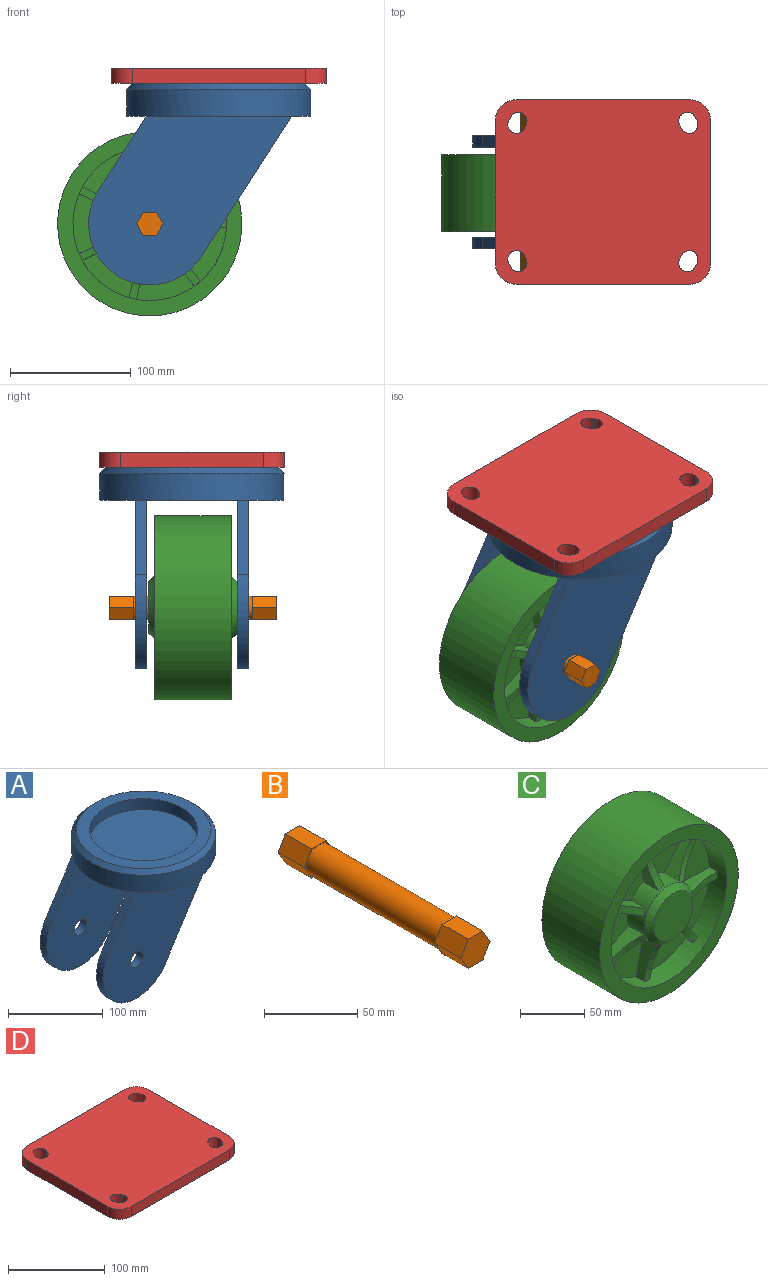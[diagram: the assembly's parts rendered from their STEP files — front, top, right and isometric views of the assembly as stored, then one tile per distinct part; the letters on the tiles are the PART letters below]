
ASSEMBLY  parts=4 mates=3
PART A: 20 faces, bbox 183.9x152.4x166.5 mm
  f0: plane 61.55x39.57mm, normal (-0.84,0,0.54), area 696.9mm2, adj f1,f3,f4,f5
  f1: cylinder r=50.58mm len=93.14mm, axis (0,1,0), area 1513.7mm2, adj f0,f2,f3,f4
  f2: plane 116.25x74.73mm, normal (0.84,0,-0.54), area 1316.4mm2, adj f1,f3,f4,f5
  f3: plane 167.87x139.48mm, normal (0,-1,0), area 14426.4mm2, adj f0,f1,f2,f8,f12
  f4: plane 167.87x139.48mm, normal (0,1,0), area 14426.4mm2, adj f0,f1,f2,f5,f12
  f5: plane 152.4x93.6mm, normal (0,0,-1), area 11017.4mm2, adj f0,f2,f4,f6,f13,f15,f17
  f6: cylinder r=76.2mm len=152.4mm, axis (0,0,-1), area 10519.2mm2, adj f5,f8,f11,f18
  f7: plane 114.3x114.3mm, normal (0,0,1), area 10260.8mm2, adj f9
  f8: plane 120.27x29.4mm, normal (0,0,-1), area 2466.5mm2, adj f3,f6
  f9: cylinder r=57.15mm len=114.3mm, axis (0,0,-1), area 5153.2mm2, adj f7,f10
  f10: plane 142.24x142.24mm, normal (0,0,1), area 5629.5mm2, adj f9,f11
  f11: cone r=76.2mm half-angle=45deg, axis (0,0,-1), area 3325mm2, adj f6,f10
  f12: cylinder r=9.53mm len=19.05mm, axis (0,1,0), area 570mm2, adj f3,f4
  f13: plane 61.55x39.57mm, normal (-0.84,0,0.54), area 696.9mm2, adj f5,f14,f16,f17
  f14: cylinder r=50.58mm len=93.14mm, axis (0,-1,0), area 1513.7mm2, adj f13,f15,f16,f17
  f15: plane 116.25x74.73mm, normal (0.84,0,-0.54), area 1316.4mm2, adj f5,f14,f16,f17
  f16: plane 167.87x139.48mm, normal (0,1,0), area 14426.4mm2, adj f13,f14,f15,f18,f19
  f17: plane 167.87x139.48mm, normal (0,-1,0), area 14426.4mm2, adj f5,f13,f14,f15,f19
  f18: plane 120.27x29.4mm, normal (0,0,-1), area 2466.5mm2, adj f6,f16
  f19: cylinder r=9.53mm len=19.05mm, axis (0,-1,0), area 570mm2, adj f16,f17
PART B: 17 faces, bbox 22x138.4x19.1 mm
  f0: cylinder r=9.5mm len=98.68mm, axis (0,1,0), area 5889.9mm2, adj f8,f16
  f1: plane 19.84x9.53mm, normal (0.87,0,0.5), area 218.3mm2, adj f2,f6,f7,f8
  f2: plane 19.84x11mm, normal (0,0,1), area 218.3mm2, adj f1,f3,f7,f8
  f3: plane 19.84x9.53mm, normal (-0.87,0,0.5), area 218.3mm2, adj f2,f4,f7,f8
  f4: plane 19.84x9.53mm, normal (-0.87,0,-0.5), area 218.3mm2, adj f3,f5,f7,f8
  f5: plane 19.84x11mm, normal (0,0,-1), area 218.3mm2, adj f4,f6,f7,f8
  f6: plane 19.84x9.53mm, normal (0.87,0,-0.5), area 218.3mm2, adj f1,f5,f7,f8
  f7: plane 22x19.05mm, normal (0,-1,0), area 314.3mm2, adj f1,f2,f3,f4,f5,f6
  f8: plane 22x19.05mm, normal (0,1,0), area 30.8mm2, adj f0,f1,f2,f3,f4,f5,f6
  f9: plane 19.84x9.53mm, normal (0.87,0,0.5), area 218.3mm2, adj f10,f14,f15,f16
  f10: plane 19.84x11mm, normal (0,0,1), area 218.3mm2, adj f9,f11,f15,f16
  f11: plane 19.84x9.53mm, normal (-0.87,0,0.5), area 218.3mm2, adj f10,f12,f15,f16
  f12: plane 19.84x9.53mm, normal (-0.87,0,-0.5), area 218.3mm2, adj f11,f13,f15,f16
  f13: plane 19.84x11mm, normal (0,0,-1), area 218.3mm2, adj f12,f14,f15,f16
  f14: plane 19.84x9.53mm, normal (0.87,0,-0.5), area 218.3mm2, adj f9,f13,f15,f16
  f15: plane 22x19.05mm, normal (0,1,0), area 314.3mm2, adj f9,f10,f11,f12,f13,f14
  f16: plane 22x19.05mm, normal (0,-1,0), area 30.8mm2, adj f0,f9,f10,f11,f12,f13,f14
PART C: 67 faces, bbox 152.4x73x152.4 mm
  f0: plane 48.08x40.82mm, normal (0,-1,0), area 1256.3mm2, adj f7,f9,f27,f32
  f1: plane 46.77x46.77mm, normal (0,-1,0), area 1256.3mm2, adj f7,f9,f24,f29
  f2: plane 49.31x38.26mm, normal (0,-1,0), area 1256.3mm2, adj f7,f9,f21,f26
  f3: plane 46.77x46.77mm, normal (0,-1,0), area 1256.3mm2, adj f7,f9,f18,f23
  f4: plane 48.08x40.82mm, normal (0,-1,0), area 1256.3mm2, adj f7,f9,f15,f20
  f5: plane 44.43x44.43mm, normal (0,-1,0), area 1256.3mm2, adj f7,f9,f13,f17
  f6: plane 43.18x43.18mm, normal (0,-1,0), area 1464.4mm2, adj f33
  f7: cylinder r=26.67mm len=53.34mm, axis (0,1,0), area 2416.2mm2, adj f0,f1,f2,f3,f4,f5,f8,f12
  f8: plane 44.43x44.43mm, normal (0,-1,0), area 1256.3mm2, adj f7,f9,f14,f30
  f9: cylinder r=63.5mm len=127mm, axis (0,1,0), area 7205.5mm2, adj f0,f1,f2,f3,f4,f5,f8,f10
  f10: plane 152.4x152.4mm, normal (0,-1,0), area 5573.8mm2, adj f9,f11
  f11: cylinder r=76.2mm len=152.4mm, axis (0,1,0), area 30402.4mm2, adj f10,f44
  f12: cylinder r=76.2mm len=37.02mm, axis (0,0,-1), area 241.2mm2, adj f7,f9,f13,f14
  f13: plane 36.94x16.28mm, normal (0,0,1), area 405.3mm2, adj f5,f7,f9,f12
  f14: plane 36.94x16.28mm, normal (0,0,-1), area 405.3mm2, adj f7,f8,f9,f12
  f15: plane 28.88x23.03mm, normal (-0.78,0,0.62), area 405.3mm2, adj f4,f7,f9,f16
  f16: cylinder r=76.2mm len=32.9mm, axis (0.78,0,-0.62), area 241.2mm2, adj f7,f9,f15,f17
  f17: plane 28.88x23.03mm, normal (0.78,0,-0.62), area 405.3mm2, adj f5,f7,f9,f16
  f18: plane 36.01x16.28mm, normal (-0.97,0,-0.22), area 405.3mm2, adj f3,f7,f9,f19
  f19: cylinder r=76.2mm len=37.5mm, axis (0.97,0,0.22), area 241.2mm2, adj f7,f9,f18,f20
  f20: plane 36.01x16.28mm, normal (0.97,0,0.22), area 405.3mm2, adj f4,f7,f9,f19
  f21: plane 33.28x16.28mm, normal (-0.43,0,-0.9), area 405.3mm2, adj f2,f7,f9,f22
  f22: cylinder r=76.2mm len=36.11mm, axis (0.43,0,0.9), area 241.2mm2, adj f7,f9,f21,f23
  f23: plane 33.28x16.28mm, normal (0.43,0,0.9), area 405.3mm2, adj f3,f7,f9,f22
  f24: plane 33.28x16.28mm, normal (0.43,0,-0.9), area 405.3mm2, adj f1,f7,f9,f25
  f25: cylinder r=76.2mm len=36.11mm, axis (-0.43,0,0.9), area 241.2mm2, adj f7,f9,f24,f26
  f26: plane 33.28x16.28mm, normal (-0.43,0,0.9), area 405.3mm2, adj f2,f7,f9,f25
  f27: plane 36.01x16.28mm, normal (0.97,0,-0.22), area 405.3mm2, adj f0,f7,f9,f28
  f28: cylinder r=76.2mm len=37.5mm, axis (-0.97,0,0.22), area 241.2mm2, adj f7,f9,f27,f29
  f29: plane 36.01x16.28mm, normal (-0.97,0,0.22), area 405.3mm2, adj f1,f7,f9,f28
  f30: plane 28.88x23.03mm, normal (0.78,0,0.62), area 405.3mm2, adj f7,f8,f9,f31
  f31: cylinder r=76.2mm len=32.9mm, axis (-0.78,0,-0.62), area 241.2mm2, adj f7,f9,f30,f32
  f32: plane 28.88x23.03mm, normal (-0.78,0,-0.62), area 405.3mm2, adj f0,f7,f9,f31
  f33: cone r=26.67mm half-angle=45deg, axis (0,1,0), area 1089.2mm2, adj f6,f7
  f34: plane 48.08x40.82mm, normal (0,1,0), area 1256.3mm2, adj f41,f43,f60,f65
  f35: plane 46.77x46.77mm, normal (0,1,0), area 1256.3mm2, adj f41,f43,f57,f62
  f36: plane 49.31x38.26mm, normal (0,1,0), area 1256.3mm2, adj f41,f43,f54,f59
  f37: plane 46.77x46.77mm, normal (0,1,0), area 1256.3mm2, adj f41,f43,f51,f56
  f38: plane 48.08x40.82mm, normal (0,1,0), area 1256.3mm2, adj f41,f43,f48,f53
  f39: plane 44.43x44.43mm, normal (0,1,0), area 1256.3mm2, adj f41,f43,f46,f50
  f40: plane 43.18x43.18mm, normal (0,1,0), area 1464.4mm2, adj f66
  f41: cylinder r=26.67mm len=53.34mm, axis (0,-1,0), area 2416.2mm2, adj f34,f35,f36,f37,f38,f39,f42,f45
  f42: plane 44.43x44.43mm, normal (0,1,0), area 1256.3mm2, adj f41,f43,f47,f63
  f43: cylinder r=63.5mm len=127mm, axis (0,-1,0), area 7205.5mm2, adj f34,f35,f36,f37,f38,f39,f42,f44
  f44: plane 152.4x152.4mm, normal (0,1,0), area 5573.8mm2, adj f11,f43
  f45: cylinder r=76.2mm len=37.02mm, axis (0,0,-1), area 241.2mm2, adj f41,f43,f46,f47
  f46: plane 36.94x16.28mm, normal (0,0,1), area 405.3mm2, adj f39,f41,f43,f45
  f47: plane 36.94x16.28mm, normal (0,0,-1), area 405.3mm2, adj f41,f42,f43,f45
  f48: plane 28.88x23.03mm, normal (-0.78,0,0.62), area 405.3mm2, adj f38,f41,f43,f49
  f49: cylinder r=76.2mm len=32.9mm, axis (0.78,0,-0.62), area 241.2mm2, adj f41,f43,f48,f50
  f50: plane 28.88x23.03mm, normal (0.78,0,-0.62), area 405.3mm2, adj f39,f41,f43,f49
  f51: plane 36.01x16.28mm, normal (-0.97,0,-0.22), area 405.3mm2, adj f37,f41,f43,f52
  f52: cylinder r=76.2mm len=37.5mm, axis (0.97,0,0.22), area 241.2mm2, adj f41,f43,f51,f53
  f53: plane 36.01x16.28mm, normal (0.97,0,0.22), area 405.3mm2, adj f38,f41,f43,f52
  f54: plane 33.28x16.28mm, normal (-0.43,0,-0.9), area 405.3mm2, adj f36,f41,f43,f55
  f55: cylinder r=76.2mm len=36.11mm, axis (0.43,0,0.9), area 241.2mm2, adj f41,f43,f54,f56
  f56: plane 33.28x16.28mm, normal (0.43,0,0.9), area 405.3mm2, adj f37,f41,f43,f55
  f57: plane 33.28x16.28mm, normal (0.43,0,-0.9), area 405.3mm2, adj f35,f41,f43,f58
  f58: cylinder r=76.2mm len=36.11mm, axis (-0.43,0,0.9), area 241.2mm2, adj f41,f43,f57,f59
  f59: plane 33.28x16.28mm, normal (-0.43,0,0.9), area 405.3mm2, adj f36,f41,f43,f58
  f60: plane 36.01x16.28mm, normal (0.97,0,-0.22), area 405.3mm2, adj f34,f41,f43,f61
  f61: cylinder r=76.2mm len=37.5mm, axis (-0.97,0,0.22), area 241.2mm2, adj f41,f43,f60,f62
  f62: plane 36.01x16.28mm, normal (-0.97,0,0.22), area 405.3mm2, adj f35,f41,f43,f61
  f63: plane 28.88x23.03mm, normal (0.78,0,0.62), area 405.3mm2, adj f41,f42,f43,f64
  f64: cylinder r=76.2mm len=32.9mm, axis (-0.78,0,-0.62), area 241.2mm2, adj f41,f43,f63,f65
  f65: plane 28.88x23.03mm, normal (-0.78,0,-0.62), area 405.3mm2, adj f34,f41,f43,f64
  f66: cone r=26.67mm half-angle=45deg, axis (0,-1,0), area 1089.2mm2, adj f40,f41
PART D: 31 faces, bbox 177.8x152.4x27.3 mm
  f0: plane 53.34x53.34mm, normal (0,0,-1), area 2234.6mm2, adj f9
  f1: plane 118.11x12.7mm, normal (-1,0,0), area 1500mm2, adj f2,f4,f19,f30
  f2: plane 177.8x152.4mm, normal (0,0,-1), area 17894.2mm2, adj f1,f3,f5,f6,f10,f11,f12,f13
  f3: plane 118.11x12.7mm, normal (1,0,0), area 1500mm2, adj f2,f4,f18,f29
  f4: plane 177.8x152.4mm, normal (0,0,1), area 26001.5mm2, adj f1,f3,f5,f10,f11,f12,f13,f14
  f5: plane 143.51x12.7mm, normal (0,-1,0), area 1822.6mm2, adj f2,f4,f18,f19
  f6: cylinder r=50.8mm len=101.6mm, axis (0,0,1), area 4661.7mm2, adj f2,f8
  f7: cylinder r=31.75mm len=63.5mm, axis (0,0,1), area 1900.2mm2, adj f8,f9
  f8: plane 101.6x101.6mm, normal (0,0,-1), area 4940.4mm2, adj f6,f7
  f9: cone r=31.75mm half-angle=45deg, axis (0,0,-1), area 1318.5mm2, adj f0,f7
  f10: cylinder r=7.14mm len=13.52mm, axis (0,0,1), area 284.8mm2, adj f2,f4,f11,f13
  f11: plane 12.7x3.18mm, normal (0.89,0.45,0), area 45.1mm2, adj f2,f4,f10,f12
  f12: cylinder r=7.14mm len=13.52mm, axis (0,0,1), area 284.8mm2, adj f2,f4,f11,f13
  f13: plane 12.7x3.18mm, normal (-0.89,-0.45,0), area 45.1mm2, adj f2,f4,f10,f12
  f14: cylinder r=7.14mm len=13.52mm, axis (0,0,1), area 284.8mm2, adj f2,f4,f15,f17
  f15: plane 12.7x3.18mm, normal (0.89,-0.45,0), area 45.1mm2, adj f2,f4,f14,f16
  f16: cylinder r=7.14mm len=13.52mm, axis (0,0,1), area 284.8mm2, adj f2,f4,f15,f17
  f17: plane 12.7x3.18mm, normal (-0.89,0.45,0), area 45.1mm2, adj f2,f4,f14,f16
  f18: cylinder r=17.14mm len=17.15mm, axis (0,0,-1), area 342mm2, adj f2,f3,f4,f5
  f19: cylinder r=17.14mm len=17.15mm, axis (0,0,1), area 342mm2, adj f1,f2,f4,f5
  f20: plane 143.51x12.7mm, normal (0,1,0), area 1822.6mm2, adj f2,f4,f29,f30
  f21: cylinder r=7.14mm len=13.52mm, axis (0,0,1), area 284.8mm2, adj f2,f4,f22,f24
  f22: plane 12.7x3.18mm, normal (0.89,-0.45,0), area 45.1mm2, adj f2,f4,f21,f23
  f23: cylinder r=7.14mm len=13.52mm, axis (0,0,1), area 284.8mm2, adj f2,f4,f22,f24
  f24: plane 12.7x3.18mm, normal (-0.89,0.45,0), area 45.1mm2, adj f2,f4,f21,f23
  f25: cylinder r=7.14mm len=13.52mm, axis (0,0,1), area 284.8mm2, adj f2,f4,f26,f28
  f26: plane 12.7x3.18mm, normal (0.89,0.45,0), area 45.1mm2, adj f2,f4,f25,f27
  f27: cylinder r=7.14mm len=13.52mm, axis (0,0,1), area 284.8mm2, adj f2,f4,f26,f28
  f28: plane 12.7x3.18mm, normal (-0.89,-0.45,0), area 45.1mm2, adj f2,f4,f25,f27
  f29: cylinder r=17.14mm len=17.15mm, axis (0,0,-1), area 342mm2, adj f2,f3,f4,f20
  f30: cylinder r=17.14mm len=17.15mm, axis (0,0,1), area 342mm2, adj f1,f2,f4,f20
PLACE A t=(-146.89,-267.18,27.6)mm
PLACE B t=(-146.89,-267.94,27.6)mm
PLACE C t=(-146.89,-267.94,27.6)mm
PLACE D t=(-146.89,-267.18,26.07)mm
MATE revolute B.f0 <-> C.f41  axis (0,1,0) through (-146.89,-267.94,27.6)mm
MATE revolute C.f33 <-> A.f12  axis (0,-1,0) through (-146.89,-304.45,27.6)mm
MATE revolute A.f6 <-> D.f9  axis (0,0,1) through (-89.74,-267.18,143.55)mm
